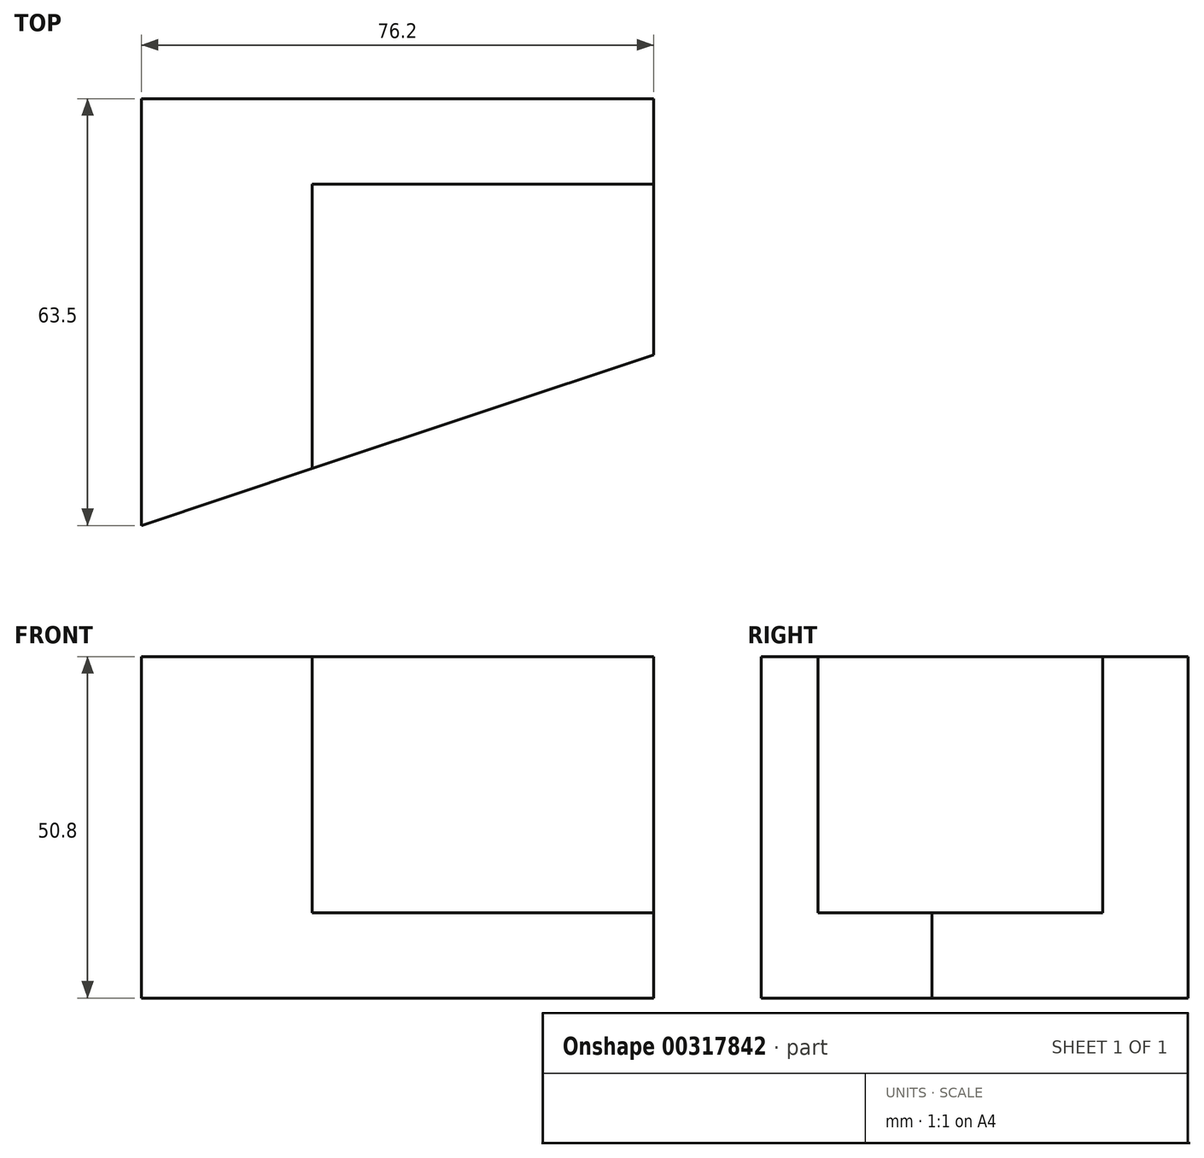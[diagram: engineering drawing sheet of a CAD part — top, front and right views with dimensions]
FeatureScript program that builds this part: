
annotation { "Feature Type Name" : "Feature", "Feature Type Description" : "" }
export const myFeature = defineFeature(function(context is Context, id is Id, definition is map)
    precondition{}
    {
        {
            var Q0;
            Q0=qCreatedBy(makeId("Front.planeOp"),FACE);
            var sketch = newSketch(context, id + "F0", { "sketchPlane" : qUnion([Q0])});
            skLineSegment(sketch, "E0", {"start": v(0, 0) * mm, "end": v(0, 50.8) * mm});
            skLineSegment(sketch, "E1", {"start": v(0, 50.8) * mm, "end": v(76.2, 50.8) * mm});
            skLineSegment(sketch, "E2", {"start": v(76.2, 50.8) * mm, "end": v(76.2, 0) * mm});
            skLineSegment(sketch, "E3", {"start": v(76.2, 0) * mm, "end": v(0, 0) * mm});
            skSolve(sketch);
        }
        {
            var Q0;
            Q0 = qSketchRegion(id + "F0", true);
            extrude(context, id + "F1", {"entities" : qUnion([Q0]), "endBound" : BoundingType.SYMMETRIC, "depth" : 63.5 * mm});
        }
        {
            var Q0;
            Q0=makeQuery(id+"F1.opExtrude","CAP_FACE",FACE,{"disambiguationData":[OSD([sQuery(id+"F0.wireOp",EDGE,"E0"),sQuery(id+"F0.wireOp",EDGE,"E1"),sQuery(id+"F0.wireOp",EDGE,"E2"),sQuery(id+"F0.wireOp",EDGE,"E3")])],"isStart":false});
            var sketch = newSketch(context, id + "F2", { "sketchPlane" : qUnion([Q0])});
            skLineSegment(sketch, "E4", {"start": v(76.2, 50.8) * mm, "end": v(25.4, 50.8) * mm});
            skLineSegment(sketch, "E5", {"start": v(25.4, 50.8) * mm, "end": v(25.4, 12.7) * mm});
            skLineSegment(sketch, "E6", {"start": v(25.4, 12.7) * mm, "end": v(76.2, 12.7) * mm});
            skLineSegment(sketch, "E7", {"start": v(76.2, 12.7) * mm, "end": v(76.2, 50.8) * mm});
            skSolve(sketch);
        }
        {
            var Q0;
            Q0 = qSketchRegion(id + "F2", true);
            extrude(context, id + "F3", {"entities" : qUnion([Q0]), "operationType" : NewBodyOperationType.REMOVE, "oppositeDirection" : true, "depth" : 50.8 * mm});
        }
        {
            var Q0;
            Q0=qCreatedBy(makeId("Top.planeOp"),FACE);
            var sketch = newSketch(context, id + "F4", { "sketchPlane" : qUnion([Q0])});
            skLineSegment(sketch, "E8", {"start": v(0, -31.75) * mm, "end": v(76.2, -31.75) * mm});
            skLineSegment(sketch, "E9", {"start": v(76.2, -31.75) * mm, "end": v(76.2, -6.35) * mm});
            skLineSegment(sketch, "E10", {"start": v(76.2, -6.35) * mm, "end": v(0, -31.75) * mm});
            skSolve(sketch);
        }
        {
            var Q0;
            Q0 = qSketchRegion(id + "F4", true);
            extrude(context, id + "F5", {"entities" : qUnion([Q0]), "operationType" : NewBodyOperationType.REMOVE, "endBound" : BoundingType.THROUGH_ALL, "depth" : 25.4 * mm});
        }
    });
